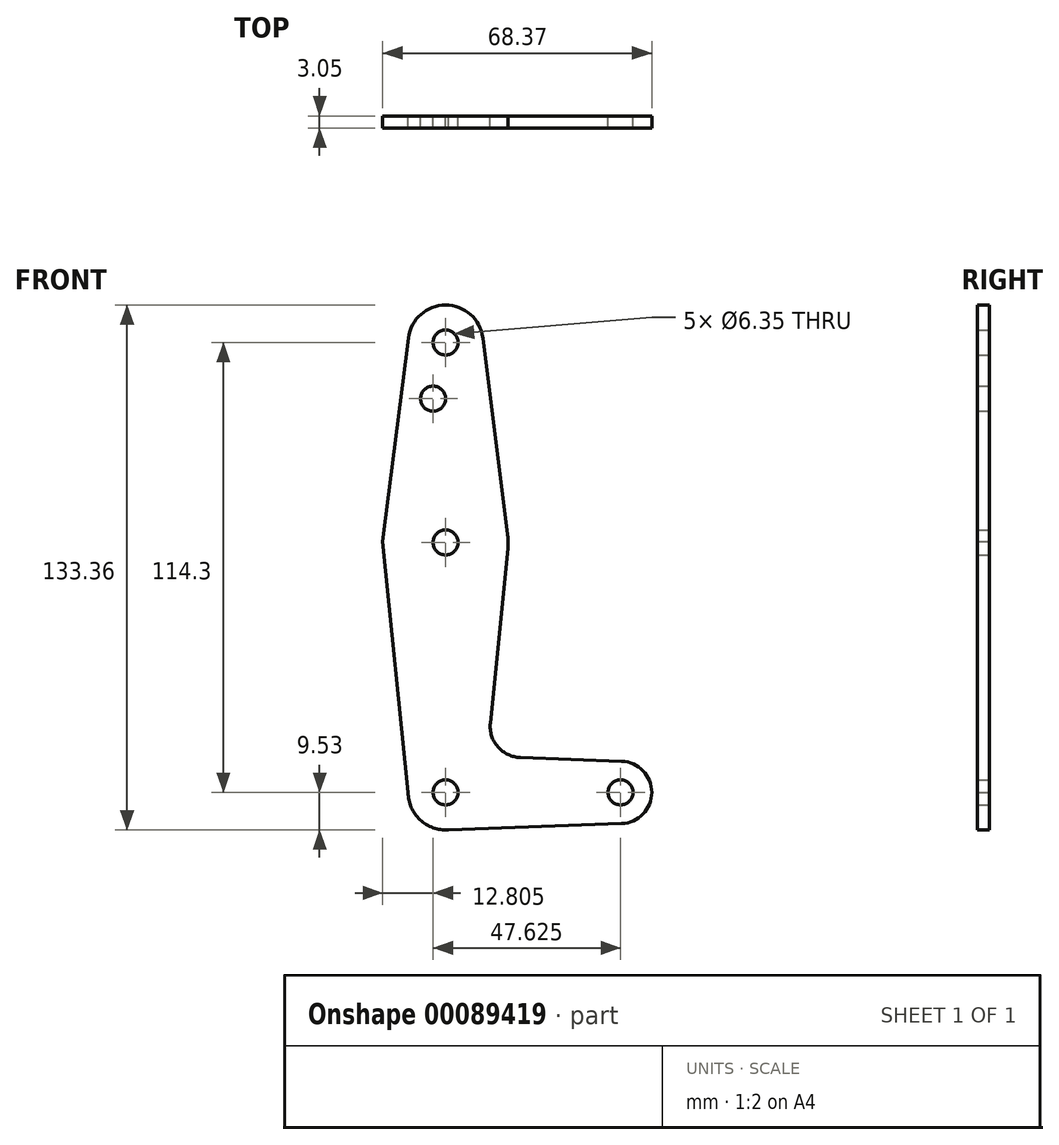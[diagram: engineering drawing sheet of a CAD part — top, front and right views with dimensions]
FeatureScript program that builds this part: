
annotation { "Feature Type Name" : "Feature", "Feature Type Description" : "" }
export const myFeature = defineFeature(function(context is Context, id is Id, definition is map)
    precondition{}
    {
        {
            var Q0;
            Q0=qCreatedBy(makeId("Front.planeOp"),FACE);
            var sketch = newSketch(context, id + "F0", { "sketchPlane" : qUnion([Q0])});
            skCircle(sketch, "E0", {"center": v(0, 114.3) * mm, "radius": 9.53 * mm});
            skCircle(sketch, "E1", {"center": v(0, 63.5) * mm, "radius": 15.88 * mm});
            skCircle(sketch, "E2", {"center": v(0, 0) * mm, "radius": 9.53 * mm});
            skCircle(sketch, "E3", {"center": v(44.45, 0) * mm, "radius": 7.94 * mm});
            skLineSegment(sketch, "E4", {"start": v(0, 114.3) * mm, "end": v(0, 63.5) * mm});
            skLineSegment(sketch, "E5", {"start": v(0, 63.5) * mm, "end": v(0, 0) * mm});
            skLineSegment(sketch, "E6", {"start": v(0, 0) * mm, "end": v(44.45, 0) * mm});
            skLineSegment(sketch, "E7", {"start": v(-9.45, 115.5) * mm, "end": v(-15.98, 63.7) * mm});
            skLineSegment(sketch, "E8", {"start": v(0, -9.53) * mm, "end": v(44.73, -7.93) * mm});
            skLineSegment(sketch, "E9", {"start": v(-9.52, 0) * mm, "end": v(-9.57, 0) * mm});
            skLineSegment(sketch, "E10", {"start": v(-9.57, 0) * mm, "end": v(-15.98, 63.7) * mm});
            skLineSegment(sketch, "E11", {"start": v(15.8, 61.91) * mm, "end": v(11.34, 17.6) * mm});
            skLineSegment(sketch, "E12", {"start": v(44.73, 7.93) * mm, "end": v(18.97, 8.85) * mm});
            skArc(sketch, "E13.filletArc", {"start": v(11.34, 17.6) * mm, "mid": v(13.26, 11.57) * mm, "end": v(18.97, 8.85) * mm});
            skCircle(sketch, "E14", {"center": v(0, 114.3) * mm, "radius": 3.18 * mm});
            skLineSegment(sketch, "E15", {"start": v(9.45, 115.5) * mm, "end": v(15.75, 65.48) * mm});
            skCircle(sketch, "E16", {"center": v(0, 63.5) * mm, "radius": 3.18 * mm});
            skCircle(sketch, "E17", {"center": v(-3.17, 100.03) * mm, "radius": 3.18 * mm});
            skCircle(sketch, "E18", {"center": v(0, 0) * mm, "radius": 3.18 * mm});
            skCircle(sketch, "E19", {"center": v(44.45, 0) * mm, "radius": 3.18 * mm});
            skSolve(sketch);
        }
        {
            var Q0;
            Q0 = qSketchRegion(id + "F0", true);
            var Q1;
            {var subQ0=sQuery(id+"F0.wireOp",EDGE,"E5");var subQ1=sQuery(id+"F0.wireOp",EDGE,"E2");var subQ2=makeQuery(id+"F0.imprint","INTERSECT",VERTEX,{"derivedFrom":[subQ1,subQ0]});Q1=makeQuery(id+"F0.imprint","IMPRINT",FACE,{"disambiguationData":[TD([[makeQuery(id+"F0.imprint","IMPRINT",EDGE,{"disambiguationData":[TD([[subQ2,1.0]])],"derivedFrom":subQ1}),1.0]])]});}
            extrude(context, id + "F1", {"entities" : qUnion([Q0, Q1]), "depth" : 3.05 * mm});
        }
        {
            var Q0;
            Q0 = qSketchRegion(id + "F0", true);
            extrude(context, id + "F2", {"entities" : qUnion([Q0]), "operationType" : NewBodyOperationType.ADD, "depth" : 3.05 * mm});
        }
    });
